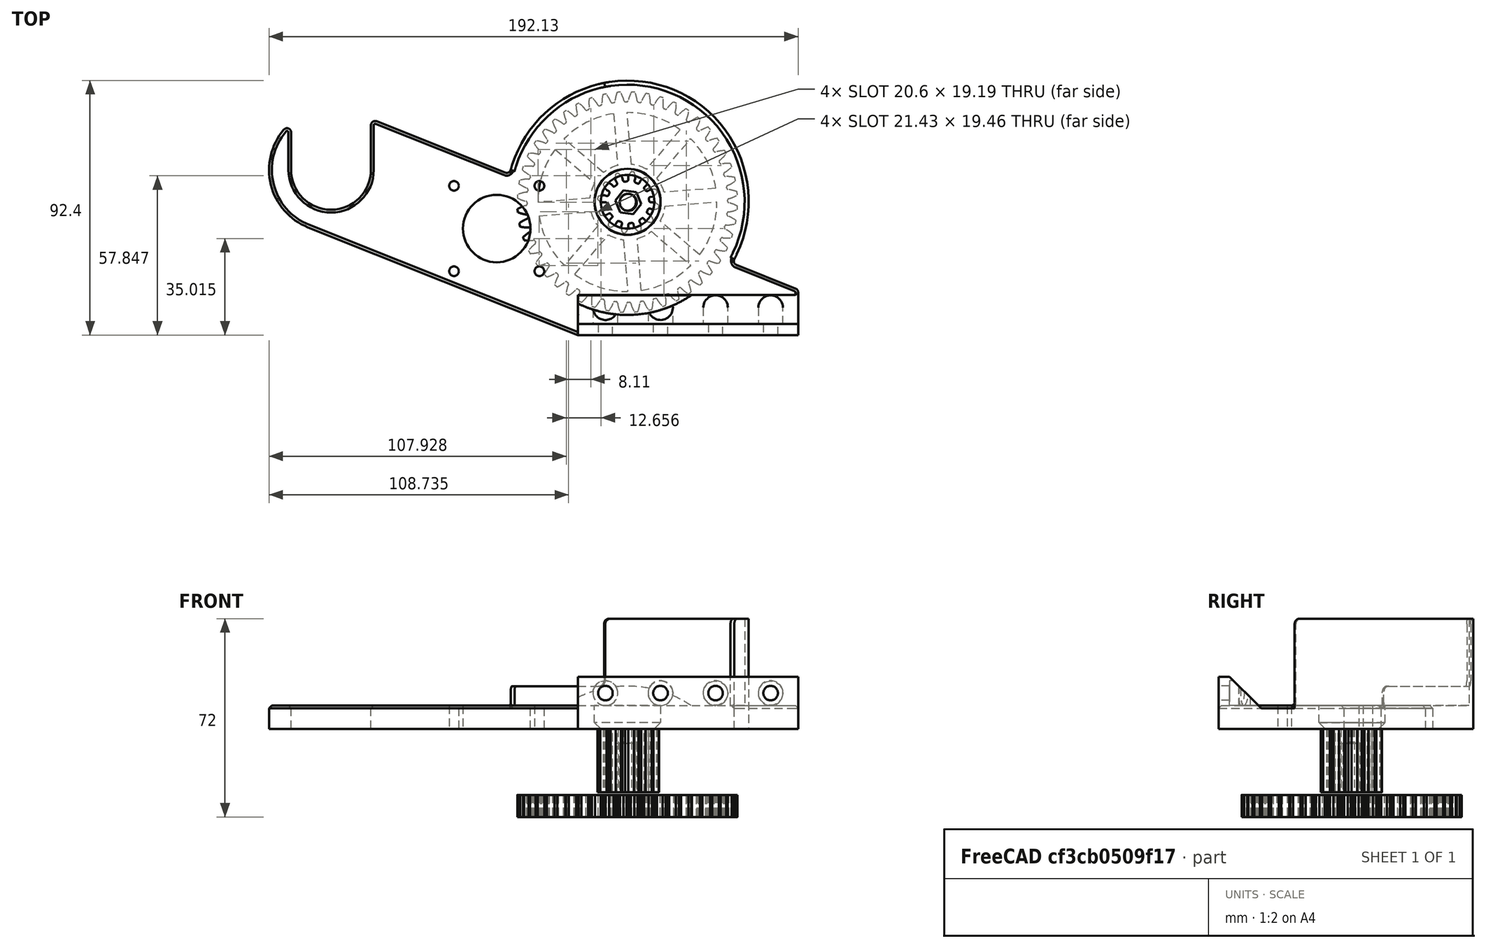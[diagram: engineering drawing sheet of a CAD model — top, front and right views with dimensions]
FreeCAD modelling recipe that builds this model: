
FCSTD DOCUMENT  (FreeCAD 0.20R29177 (Git))
Label: 23343BBA5B_Autotruder Leftward Spool and Gear Holder REV A
License: All rights reserved
LicenseURL: http://en.wikipedia.org/wiki/All_rights_reserved
objects: Sketcher::SketchObject×7, PartDesign::Pad×3, PartDesign::Pocket×3, PartDesign::Chamfer×3, PartDesign::Fillet×3, Part::Feature×2, PartDesign::Plane×2, PartDesign::SubtractiveCylinder×2, App::Part×1, Mesh::Feature×1, PartDesign::Body×1
note: 40 computed .brp shape members not serialized (recipe doc carries the construction recipe); baked Part::Feature solids carry a one-line shape summary decoded from their .brp

FEATURE [Sketcher::SketchObject] Sketch002
  FullyConstrained = false
  MapMode = 5
  sketch-geometry (26):
    g0: ArcOfCircle CenterX=-129.63 CenterY=60 CenterZ=0 NormalX=0 NormalY=0 NormalZ=1 AngleXU=0 Radius=14.5 StartAngle=3.14159 EndAngle=6.28317
    g1: ArcOfCircle CenterX=-129.63 CenterY=60 CenterZ=0 NormalX=0 NormalY=0 NormalZ=1 AngleXU=0 Radius=22.5 StartAngle=2.43705 EndAngle=4.33263
    g2: LineSegment StartX=-40 StartY=0 StartZ=0 EndX=40 EndY=0 EndZ=0
    g3: LineSegment StartX=40 StartY=0 StartZ=0 EndX=40 EndY=15.5052 EndZ=0
    g4: LineSegment StartX=-40 StartY=0 StartZ=0 EndX=-137.971 EndY=39.103 EndZ=0
    g5: LineSegment StartX=-113.074 StartY=77.618 StartZ=0 EndX=-66.4027 EndY=58.9901 EndZ=0
    g6: Circle CenterX=-69.469 CenterY=38.6797 CenterZ=0 NormalX=0 NormalY=0 NormalZ=1 AngleXU=0 Radius=12.25
    g7: Circle CenterX=-21.953 CenterY=48.4 CenterZ=0 NormalX=0 NormalY=0 NormalZ=1 AngleXU=0 Radius=9.75
    g8: LineSegment StartX=-144.13 StartY=60 StartZ=0 EndX=-144.13 EndY=73.6015 EndZ=0
    g9: LineSegment StartX=-115.13 StartY=59.9997 StartZ=0 EndX=-115.13 EndY=76.2248 EndZ=0
    g10: ArcOfCircle CenterX=-145.63 CenterY=73.6015 CenterZ=0 NormalX=0 NormalY=0 NormalZ=1 AngleXU=0 Radius=1.5 StartAngle=3e-15 EndAngle=2.43705
    g11: ArcOfCircle CenterX=-113.63 CenterY=76.2248 CenterZ=0 NormalX=0 NormalY=0 NormalZ=1 AngleXU=0 Radius=1.5 StartAngle=1.19104 EndAngle=3.14159
    g12: ArcOfCircle CenterX=38.5 CenterY=15.5052 CenterZ=0 NormalX=0 NormalY=0 NormalZ=1 AngleXU=0 Radius=1.5 StartAngle=0 EndAngle=1.19104
    g13: ArcOfCircle CenterX=-21.953 CenterY=48.4 CenterZ=0 NormalX=0 NormalY=0 NormalZ=1 AngleXU=0 Radius=44 StartAngle=5.79018 EndAngle=9.15827
    g14: LineSegment StartX=17.5726 StartY=25.473 StartZ=0 EndX=39.056 EndY=16.8983 EndZ=0
    g15: ArcOfCircle CenterX=18.1287 CenterY=26.8661 CenterZ=0 NormalX=0 NormalY=0 NormalZ=1 AngleXU=0 Radius=1.5 StartAngle=2.64859 EndAngle=4.33263
    g16: ArcOfCircle CenterX=-65.8467 CenterY=60.3832 CenterZ=0 NormalX=0 NormalY=0 NormalZ=1 AngleXU=0 Radius=1.5 StartAngle=4.33263 EndAngle=6.01667
    g17: LineSegment StartX=-53.969 StartY=23.1797 StartZ=0 EndX=-53.969 EndY=54.1797 EndZ=0
    g18: LineSegment StartX=-53.969 StartY=54.1797 StartZ=0 EndX=-84.969 EndY=54.1797 EndZ=0
    g19: LineSegment StartX=-84.969 StartY=54.1797 StartZ=0 EndX=-84.969 EndY=23.1797 EndZ=0
    g20: LineSegment StartX=-84.969 StartY=23.1797 StartZ=0 EndX=-53.969 EndY=23.1797 EndZ=0
    g21: GeomPoint X=-69.469 Y=38.6797 Z=0
    g22: Circle CenterX=-84.969 CenterY=23.1797 CenterZ=0 NormalX=0 NormalY=0 NormalZ=1 AngleXU=0 Radius=1.75
    g23: Circle CenterX=-84.969 CenterY=54.1797 CenterZ=0 NormalX=0 NormalY=0 NormalZ=1 AngleXU=0 Radius=1.75
    g24: Circle CenterX=-53.969 CenterY=54.1797 CenterZ=0 NormalX=0 NormalY=0 NormalZ=1 AngleXU=0 Radius=1.75
    g25: Circle CenterX=-53.969 CenterY=23.1797 CenterZ=0 NormalX=0 NormalY=0 NormalZ=1 AngleXU=0 Radius=1.75
  constraints (64):
    c: Diameter(g0) = 29
    c: Coincident(g1,g0)
    c: Diameter(g1) = 45
    c: PointOnObject(g2,g-1)
    c: PointOnObject(g2,g-1)
    c: Vertical(g3)
    c: DistanceX(g0) = -129.63
    c: DistanceY(g-1,g0) = 60
    c: Parallel(g5,g4)
    c: Diameter(g6) = 24.5
    c: Diameter(g7) = 19.5
    c: Distance(g7,g0) = 108.3
    c: Distance(g6,g7) = 48.5
    c: DistanceY(g4,g7) = 48.4
    c: Vertical(g8)
    c: Tangent(g0,g8) = 1.5708
    c: Vertical(g9)
    c: Tangent(g1,g4) = 1.5708
    c: Tangent(g8,g10) = -1.5708
    c: Tangent(g1,g10) = -1.5708
    c: Diameter(g10) = 3
    c: Tangent(g5,g11) = 1.5708
    c: Tangent(g9,g11) = 1.5708
    c: Diameter(g11) = 3
    c: Tangent(g3,g12) = -1.5708
    c: Diameter(g12) = 3
    c: DistanceX(g2,g-1) = 40
    c: DistanceX(g2,g2) = 80
    c: Coincident(g4,g2)
    c: Distance(g6,g4) = 25
    c: Coincident(g9,g0)
    c: Distance(g2,g5) = 45
    c: Coincident(g3,g2)
    c: Tangent(g13,g15) = 1.5708
    c: Tangent(g14,g15) = -1.5708
    c: Tangent(g13,g16) = 1.5708
    c: Tangent(g5,g16) = -1.5708
    c: Equal(g12,g15)
    c: Equal(g15,g16)
    c: Diameter(g13) = 88
    c: Coincident(g7,g13)
    c: PointOnObject(g14,g5)
    c: PointOnObject(g12,g5)
    c: Tangent(g14,g12) = 1.5708
    c: Coincident(g17,g18)
    c: Coincident(g18,g19)
    c: Coincident(g19,g20)
    c: Coincident(g20,g17)
    c: Horizontal(g18)
    c: Horizontal(g20)
    c: Vertical(g17)
    c: Vertical(g19)
    c: Symmetric(g18,g17,g21)
    c: Coincident(g21,g6)
    c: DistanceX(g18,g18) = 31
    c: Equal(g18,g19)
    c: Coincident(g22,g19)
    c: Coincident(g23,g18)
    c: Coincident(g24,g17)
    c: Coincident(g25,g17)
    c: Equal(g22,g23)
    c: Equal(g23,g24)
    c: Equal(g24,g25)
    c: Diameter(g22) = 3.5
FEATURE [PartDesign::Pad] Pad  label="BaseBad"
  Direction = (0,0,1)
  Length = 8.425
  Length2 = 10
  Profile = -> Sketch002
  ReferenceAxis = -> Sketch002 [N_Axis]
  Type = 0
FEATURE [Part::Feature] Part__Feature  label="PolarPattern"
  Placement = pos=(-22,48.3,-9) rot=(0,0,1;1.64934rad)
  shape: bbox 79.95 x 79.95 x 8 mm, 323 faces (baked)
FEATURE [Part::Feature] Part__Feature001  label="Cut002"
  Placement = pos=(-21.7,48.2,0) rot=(0,0,-1;0.143117rad)
  shape: bbox 22.29 x 22.29 x 23 mm, 106 faces (baked)
FEATURE [App::Part] TOP___Part_5C___DoubleGear48t
  Group = -> [Part__Feature,Part__Feature001]
  Origin = -> Origin001
  Placement = pos=(0,0,38) rot=(0,0,1;0rad)
FEATURE [Sketcher::SketchObject] Sketch
  ExternalGeometry = -> [Pad]
  FullyConstrained = false
  MapMode = 5
  Support = -> [XY_Plane]
  sketch-geometry (4):
    g0: ArcOfCircle CenterX=-21.9529 CenterY=48.4002 CenterZ=0 NormalX=0 NormalY=0 NormalZ=1 AngleXU=0 Radius=42.51 StartAngle=5.78619 EndAngle=9.16226
    g1: LineSegment StartX=-64.3996 StartY=59.9882 StartZ=0 EndX=-63.0065 EndY=59.4321 EndZ=0
    g2: LineSegment StartX=15.4142 StartY=28.1321 StartZ=0 EndX=16.8073 EndY=27.576 EndZ=0
    g3: ArcOfCircle CenterX=-21.9529 CenterY=48.4002 CenterZ=0 NormalX=0 NormalY=0 NormalZ=1 AngleXU=0 Radius=44 StartAngle=5.79018 EndAngle=9.15827
  constraints (10):
    c: Coincident(g1,g-3)
    c: Coincident(g2,g-3)
    c: Coincident(g0,g1)
    c: Coincident(g0,g2)
    c: Equal(g1,g2)
    c: Distance(g1) = 1.5
    c: Parallel(g1,g2)
    c: Coincident(g3,g0)
    c: Coincident(g3,g2)
    c: Coincident(g3,g1)
FEATURE [PartDesign::Pad] Pad001  label="PadGuard"
  BaseFeature = -> Pad
  Direction = (0,0,1)
  Length = 40
  Length2 = 10
  Profile = -> Sketch
  ReferenceAxis = -> Sketch [N_Axis]
  Type = 0
FEATURE [Mesh::Feature] RECREATOR3D___Part_8___Small_Gear_WIDER  label="RECREATOR3D - Part 8 - Small Gear WIDER"
  Placement = pos=(-69.3,38.6,8) rot=(0,0,1;0.106465rad)
FEATURE [Sketcher::SketchObject] Sketch003
  ExternalGeometry = -> [Pad001]
  FullyConstrained = true
  MapMode = 5
  Placement = pos=(0,0,0) rot=(0.57735,0.57735,0.57735;2.0944rad)
  Support = -> [YZ_Plane]
  sketch-geometry (4):
    g0: LineSegment StartX=0 StartY=18.925 StartZ=0 EndX=4 EndY=18.925 EndZ=0
    g1: LineSegment StartX=4 StartY=18.925 StartZ=0 EndX=14.5 EndY=8.425 EndZ=0
    g2: LineSegment StartX=0 StartY=8.425 StartZ=0 EndX=14.5 EndY=8.425 EndZ=0
    g3: LineSegment StartX=0 StartY=18.925 StartZ=0 EndX=0 EndY=8.425 EndZ=0
  constraints (11):
    c: PointOnObject(g0,g-2)
    c: Horizontal(g0)
    c: Coincident(g1,g0)
    c: PointOnObject(g1,g-3)
    c: Angle(g0,g1) = 2.35619
    c: DistanceX(g0,g0) = 4
    c: Coincident(g2,g-3)
    c: Coincident(g2,g1)
    c: Coincident(g3,g0)
    c: DistanceY(g3,g3) = 10.5
    c: Coincident(g3,g2)
FEATURE [PartDesign::Pad] Pad002  label="PadFoot"
  BaseFeature = -> Pad001
  Direction = (1,-2e-16,3e-16)
  Length = 40
  Length2 = 40
  Profile = -> Sketch003
  ReferenceAxis = -> Sketch003 [N_Axis]
  Type = 4
FEATURE [Sketcher::SketchObject] Sketch004
  ExternalGeometry = -> [Pad002]
  FullyConstrained = false
  MapMode = 5
  Placement = pos=(0,0,0) rot=(1,0,0;1.5708rad)
  Support = -> [XZ_Plane]
  sketch-geometry (7):
    g0: Circle CenterX=30 CenterY=12.97 CenterZ=0 NormalX=0 NormalY=0 NormalZ=1 AngleXU=0 Radius=2.65
    g1: Circle CenterX=10 CenterY=12.97 CenterZ=0 NormalX=0 NormalY=0 NormalZ=1 AngleXU=0 Radius=2.65
    g2: LineSegment StartX=30 StartY=12.97 StartZ=0 EndX=10 EndY=12.97 EndZ=0
    g3: Circle CenterX=-10 CenterY=12.97 CenterZ=0 NormalX=0 NormalY=0 NormalZ=1 AngleXU=0 Radius=2.65
    g4: LineSegment StartX=10 StartY=12.97 StartZ=0 EndX=-10 EndY=12.97 EndZ=0
    g5: Circle CenterX=-30 CenterY=12.97 CenterZ=0 NormalX=0 NormalY=0 NormalZ=1 AngleXU=0 Radius=2.65
    g6: LineSegment StartX=-10 StartY=12.97 StartZ=0 EndX=-30 EndY=12.97 EndZ=0
  constraints (17):
    c: Diameter(g0) = 5.3
    c: Diameter(g1) = 5.3
    c: Coincident(g0,g2)
    c: Coincident(g1,g2)
    c: Distance(g2) = 20
    c: Angle(g2) = 3.14159
    c: Diameter(g3) = 5.3
    c: Coincident(g1,g4)
    c: Coincident(g3,g4)
    c: Equal(g2,g4)
    c: Parallel(g4,g2)
    c: Diameter(g5) = 5.3
    c: Coincident(g3,g6)
    c: Coincident(g5,g6)
    c: Equal(g2,g6)
    c: Parallel(g6,g2)
    c: DistanceY(g-1,g0) = 12.97
FEATURE [PartDesign::Pocket] Pocket
  BaseFeature = -> Pad002
  Direction = (0,1,2e-16)
  Length = 18
  Length2 = 5
  Profile = -> Sketch004
  ReferenceAxis = -> Sketch004 [N_Axis]
  Type = 0
FEATURE [PartDesign::Plane] DatumPlane  label="CounterBorePlane"
  AttachmentOffset = pos=(0,0,-4) rot=(0,0,1;0rad)
  Length = 214.48
  MapMode = 5
  Placement = pos=(9e-16,4,-9e-16) rot=(1,0,0;1.5708rad)
  ResizeMode = 0
  Support = -> [Pocket]
  Width = 87.3503
FEATURE [Sketcher::SketchObject] Sketch005  label="ScrewholeSketch"
  ExternalGeometry = -> [Pocket]
  FullyConstrained = false
  MapMode = 5
  Placement = pos=(9e-16,4,-9e-16) rot=(1,0,0;1.5708rad)
  Support = -> [DatumPlane]
  sketch-geometry (4):
    g0: Circle CenterX=-30 CenterY=12.975 CenterZ=0 NormalX=0 NormalY=0 NormalZ=1 AngleXU=0 Radius=4.5
    g1: Circle CenterX=-10 CenterY=12.97 CenterZ=0 NormalX=0 NormalY=0 NormalZ=1 AngleXU=0 Radius=4.5
    g2: Circle CenterX=30 CenterY=12.97 CenterZ=0 NormalX=0 NormalY=0 NormalZ=1 AngleXU=0 Radius=4.5
    g3: Circle CenterX=10 CenterY=12.97 CenterZ=0 NormalX=0 NormalY=0 NormalZ=1 AngleXU=0 Radius=4.5
  constraints (7):
    c: Coincident(g1,g-4)
    c: Coincident(g2,g-5)
    c: Coincident(g3,g-6)
    c: Diameter(g3) = 9
    c: Equal(g3,g2)
    c: Equal(g2,g1)
    c: Equal(g1,g0)
FEATURE [PartDesign::Pocket] Pocket001
  BaseFeature = -> Pocket
  Direction = (2e-16,1,-2e-16)
  Length = 12
  Length2 = 5
  Profile = -> Sketch005
  ReferenceAxis = -> Sketch005 [N_Axis]
  Type = 0
FEATURE [Sketcher::SketchObject] Sketch006
  FullyConstrained = true
  MapMode = 5
  Support = -> [XY_Plane]
FEATURE [PartDesign::Plane] DatumPlane001
  Length = 222.162
  MapMode = 5
  Placement = pos=(0,0,8.425) rot=(0,0,1;0rad)
  ResizeMode = 0
  Support = -> [Pad001]
  Width = 147.395
FEATURE [Sketcher::SketchObject] Sketch007
  ExternalGeometry = -> [Pad001]
  FullyConstrained = true
  MapMode = 5
  Placement = pos=(0,0,8.425) rot=(0,0,1;0rad)
  Support = -> [DatumPlane001]
  sketch-geometry (1):
    g0: Circle CenterX=-21.953 CenterY=48.4 CenterZ=0 NormalX=0 NormalY=0 NormalZ=1 AngleXU=0 Radius=12
  constraints (2):
    c: Coincident(g0,g-3)
    c: Diameter(g0) = 24
FEATURE [PartDesign::Pocket] Pocket002
  BaseFeature = -> Pocket001
  Direction = (0,0,-1)
  Length = 6.2
  Length2 = 5
  Profile = -> Sketch007
  ReferenceAxis = -> Sketch007 [N_Axis]
  Type = 0
FEATURE [PartDesign::Chamfer] Chamfer
  Angle = 45
  Base = -> Pocket002 [Edge72]
  BaseFeature = -> Pocket002
  ChamferType = 0
  FlipDirection = false
  Size = 2.2
  Size2 = 1
  SupportTransform = false
  UseAllEdges = false
FEATURE [PartDesign::Fillet] Fillet
  Base = -> Chamfer [Edge93,Edge101]
  BaseFeature = -> Chamfer
  Radius = 2
  SupportTransform = false
  UseAllEdges = false
FEATURE [PartDesign::Chamfer] Chamfer001
  Angle = 45
  Base = -> Fillet [Edge29,Edge27,Edge28]
  BaseFeature = -> Fillet
  ChamferType = 0
  FlipDirection = false
  Size = 1
  Size2 = 1
  SupportTransform = false
  UseAllEdges = false
FEATURE [PartDesign::Chamfer] Chamfer002
  Angle = 45
  Base = -> Chamfer001 [Edge64]
  BaseFeature = -> Chamfer001
  ChamferType = 0
  FlipDirection = false
  Size = 1
  Size2 = 1
  SupportTransform = false
  UseAllEdges = false
FEATURE [PartDesign::SubtractiveCylinder] Cylinder
  Angle = 360
  AttacherType = Attacher::AttachEngine3D
  AttachmentOffset = pos=(0,0,-14.5) rot=(0,0,1;0rad)
  BaseFeature = -> Chamfer002
  FirstAngle = 0
  Height = 40
  MapMode = 2
  Placement = pos=(-129.6,60,15.5) rot=(0,0,1;0.07854rad)
  Radius = 104
  SecondAngle = 0
FEATURE [PartDesign::Fillet] Fillet001
  Base = -> Cylinder [Edge28,Edge27]
  BaseFeature = -> Cylinder
  Placement = pos=(-129.6,60,15.5) rot=(0,0,1;0.07854rad)
  Radius = 2
  SupportTransform = false
  UseAllEdges = false
FEATURE [PartDesign::Fillet] Fillet002
  Base = -> Fillet001 [Edge16]
  BaseFeature = -> Fillet001
  Placement = pos=(-129.6,60,15.5) rot=(0,0,1;0.07854rad)
  Radius = 2
  SupportTransform = false
  UseAllEdges = false
FEATURE [PartDesign::SubtractiveCylinder] Cylinder001
  Angle = 360
  AttacherType = Attacher::AttachEngine3D
  AttachmentOffset = pos=(0,0,17.44) rot=(0,0,1;0rad)
  BaseFeature = -> Fillet002
  FirstAngle = 0
  Height = 10
  MapMode = 2
  Placement = pos=(-22,48.3,8.44) rot=(0,0,1;1.64934rad)
  Radius = 41
  SecondAngle = 0
  Support = -> [Part__Feature]
FEATURE [PartDesign::Body] Body
  Group = -> [Sketch002,Pad,Sketch,Pad001,Sketch003,Pad002,Sketch004,Pocket,DatumPlane,Sketch005,Pocket001,Sketch006,DatumPlane001,Sketch007,Pocket002,Chamfer,Fillet,Chamfer001,Chamfer002,Cylinder,Fillet001,Fillet002,Cylinder001]
  Origin = -> Origin
  Tip = -> Cylinder001
